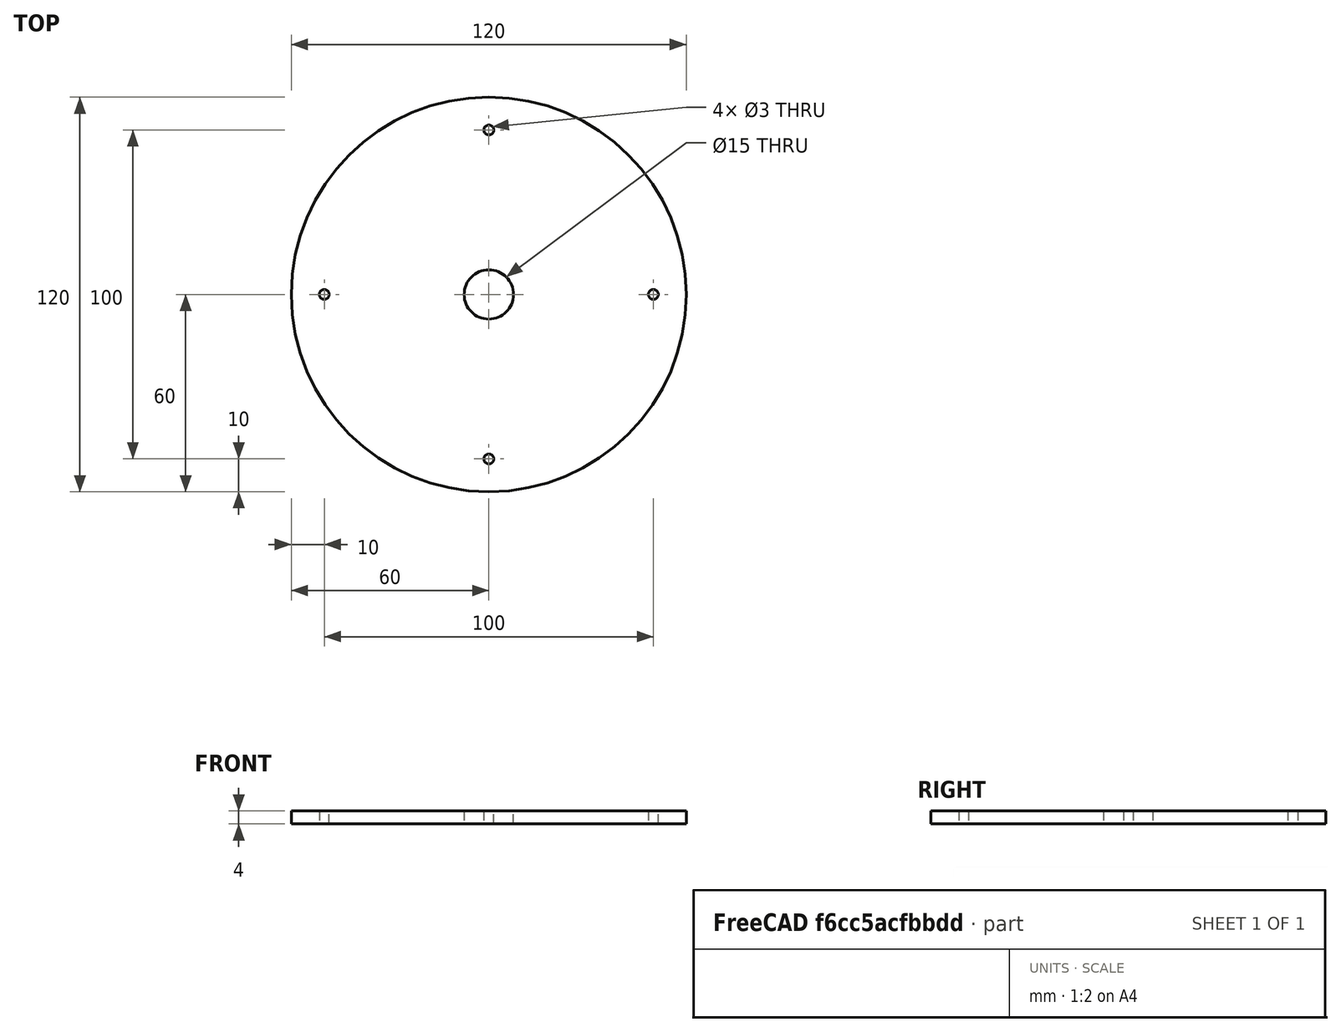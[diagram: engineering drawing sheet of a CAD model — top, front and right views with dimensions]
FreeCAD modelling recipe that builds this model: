
FCSTD DOCUMENT  (FreeCAD 0.19R24276 (Git))
Label: circle_seal_holder_part2
License: All rights reserved
LicenseURL: http://en.wikipedia.org/wiki/All_rights_reserved
objects: Sketcher::SketchObject×1, PartDesign::Pad×1, PartDesign::Body×1
note: 4 computed .brp shape members not serialized (recipe doc carries the construction recipe); baked Part::Feature solids carry a one-line shape summary decoded from their .brp

FEATURE [Sketcher::SketchObject] Sketch
  FullyConstrained = true
  MapMode = 5
  Support = -> [XY_Plane]
  sketch-geometry (11):
    g0: Circle CenterX=0 CenterY=0 CenterZ=0 NormalX=0 NormalY=0 NormalZ=1 AngleXU=0 Radius=7.5
    g1: Circle CenterX=0 CenterY=0 CenterZ=0 NormalX=0 NormalY=0 NormalZ=1 AngleXU=0 Radius=60
    g2: Circle CenterX=0 CenterY=50 CenterZ=0 NormalX=0 NormalY=0 NormalZ=1 AngleXU=0 Radius=1.5
    g3: Circle CenterX=0 CenterY=-50 CenterZ=0 NormalX=0 NormalY=0 NormalZ=1 AngleXU=0 Radius=1.5
    g4: Circle CenterX=50 CenterY=0 CenterZ=0 NormalX=0 NormalY=0 NormalZ=1 AngleXU=0 Radius=1.5
    g5: Circle CenterX=-50 CenterY=0 CenterZ=0 NormalX=0 NormalY=0 NormalZ=1 AngleXU=0 Radius=1.5
    g6: Circle CenterX=0 CenterY=0 CenterZ=0 NormalX=0 NormalY=0 NormalZ=1 AngleXU=0 Radius=50
    g7: LineSegment StartX=0 StartY=0 StartZ=0 EndX=-50 EndY=0 EndZ=0
    g8: LineSegment StartX=0 StartY=0 StartZ=0 EndX=0 EndY=50 EndZ=0
    g9: LineSegment StartX=0 StartY=0 StartZ=0 EndX=50 EndY=0 EndZ=0
    g10: LineSegment StartX=0 StartY=0 StartZ=0 EndX=0 EndY=-50 EndZ=0
  constraints (26):
    c: Coincident(g0,g-1)
    c: Diameter(g0) = 15
    c: Coincident(g1,g0)
    c: Diameter(g1) = 120
    c: PointOnObject(g2,g-2)
    c: PointOnObject(g3,g-2)
    c: PointOnObject(g4,g-1)
    c: PointOnObject(g5,g-1)
    c: Diameter(g2) = 3
    c: Equal(g2,g5)
    c: Equal(g2,g3)
    c: Equal(g2,g4)
    c: Coincident(g6,g0)
    c: Coincident(g7,g0)
    c: Coincident(g8,g0)
    c: Coincident(g9,g0)
    c: Coincident(g10,g0)
    c: PointOnObject(g10,g6)
    c: PointOnObject(g7,g6)
    c: PointOnObject(g8,g6)
    c: PointOnObject(g9,g6)
    c: Coincident(g5,g7)
    c: Coincident(g2,g8)
    c: Coincident(g4,g9)
    c: Coincident(g3,g10)
    c: Diameter(g6) = 100  '1'
FEATURE [PartDesign::Pad] Pad
  Direction = (1,1,1)
  Length = 4
  Length2 = 100
  Profile = -> Sketch
  Type = 0
FEATURE [PartDesign::Body] Body
  Group = -> [Sketch,Pad]
  Origin = -> Origin
  Tip = -> Pad
